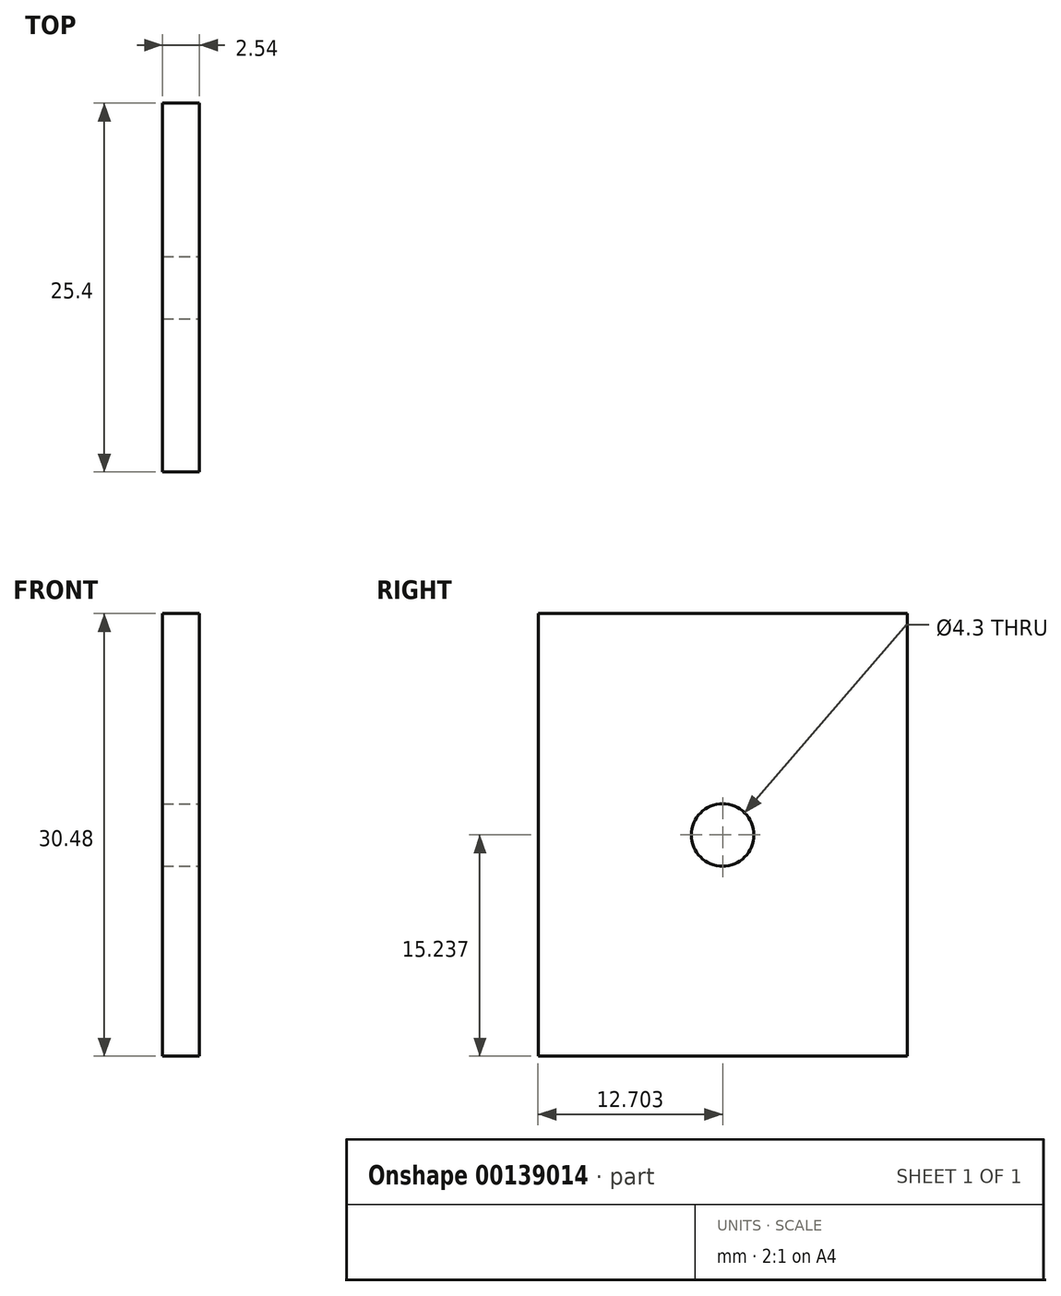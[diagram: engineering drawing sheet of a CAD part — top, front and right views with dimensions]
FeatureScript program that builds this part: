
annotation { "Feature Type Name" : "Feature", "Feature Type Description" : "" }
export const myFeature = defineFeature(function(context is Context, id is Id, definition is map)
    precondition{}
    {
        {
            var Q0;
            Q0=qCreatedBy(makeId("Right.planeOp"),FACE);
            var sketch = newSketch(context, id + "F0", { "sketchPlane" : qUnion([Q0])});
            skLineSegment(sketch, "E0", {"start": v(-48.36, 56.17) * mm, "end": v(-48.36, 25.69) * mm});
            skLineSegment(sketch, "E1", {"start": v(-48.36, 25.69) * mm, "end": v(-22.96, 25.69) * mm});
            skLineSegment(sketch, "E2", {"start": v(-22.96, 25.69) * mm, "end": v(-22.96, 56.17) * mm});
            skLineSegment(sketch, "E3", {"start": v(-22.96, 56.17) * mm, "end": v(-48.36, 56.17) * mm});
            skCircle(sketch, "E4", {"center": v(-35.66, 40.93) * mm, "radius": 2.15 * mm});
            skSolve(sketch);
        }
        {
            var Q0;
            Q0 = qSketchRegion(id + "F0", true);
            extrude(context, id + "F1", {"entities" : qUnion([Q0]), "oppositeDirection" : true, "depth" : 2.54 * mm});
        }
    });
